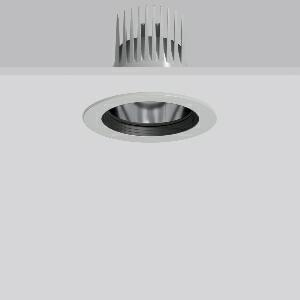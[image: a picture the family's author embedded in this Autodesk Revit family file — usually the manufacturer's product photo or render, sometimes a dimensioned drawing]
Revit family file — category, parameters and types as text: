
# Revit family: heledon_maxi_e_901759_004_2_2500
name_source: partatom
category: Lighting Fixtures
units: mm (PartAtom-declared; Revit-internal decimal feet)

## family parameters
Cut with Voids When Loaded = No
Host = Face
Light Source = No
Part Type = Normal
Room Calculation Point = No
Round Connector Dimension = Use Diameter
Shared = No

## types (1)
- HELEDON maxi E (1 x LED Modul 927, 3050 lm, 2700)
    Apparent Load = 25 VA
    Approval mark = CE
    CIE Flux Codes = 97 100 100 100 100
    Color Rendering = 92
    Color Temperature = 2700
    Default Elevation = 1800 mm
    Description = Series: HELEDON maxi
Round recessed downlight. Housing: die-cast aluminium, powder-coated. Black plastic ring and recessed LED to prevent glare from the side. Optical assembly with reflector made of MIRO-Silver with 98% total light reflection for outstanding efficiency - can be changed without tools. Best colour rendering index Ra>90. Suitable for Recessed ceiling mounting. Installation without tools thanks to spring fastening system. Including separate LED converter with connecting cable 600 mm.High quality converter without flickering and stroboscopic effect. Through-wiring box (5 pole) available as accessory. The following accessories can be mounted without use of tools: interchangeable lenses, decorative glasses, honeycomb louvre, clear and frosted diffusers, white interchangeable plastic ring. 
Colour: silver
Diameter: 162 mm
Height: 3 mm
Cut-out diameter: 152 mm
Recess height: 200 mm
Luminaire: recess height: 135 mm
Lamp: LED
Socket: without socket
Colour temperature: 2700K
Colour rendering index (CRI): 92
System power: 25 W
Rated luminous flux: 3050 lm
Luminous efficiency: 122 lm/W
Control gear: Regulated power supply
Protection class: II
Type of protection: IP 20
    Height = 0 mm  [stored 0 ft]
    Lamp = 1 x LED Modul 927
    Lamp Light Flux = 3050 lm
    Lamp count = 1
    Length = 162 mm
    Lifetime = 50000 h
    Luminous efficacy = 122 lm/W
    Manufacturer = RZB
    ModVariant = No
    Model = 901759.004.2
    Mounting Place = Ceiling
    Mounting Type = Recessed
    Number of Poles = 1
    OnlyDefault = Yes
    Power Factor = 1
    Product Name = HELEDON maxi E
    Product group = Recessed downlights
    ProductGroupID = 402
    Protection Class = Protection class II
    Protection Degree = IP 20
    RLX_Detail_Level = 1
    RLX_Emergency_Light_Flux = 0 lm
    RLX_Emergency_Type = 0
    RLX_Emergency_Type_DB = No
    RlxData = <blob elided: 118725 chars, md5=e2c16438>
    Socket = socket
    Standby Power = 0 W
    System Light Flux = 3050 lm
    System Power = 25 W
    Type Comments = Product without accessories
    Type Image = 901662.004.jpg
    URL = http://relux.com
    VarID = ---
    Voltage = 230 V
    Voltage Range = 220-240 V
    Weight = 0.00 kg
    Width = 0 mm  [stored 0 ft]

note: [stored X ft] marks values corroborated as IEEE doubles in the binary element streams (Revit-internal decimal feet)

## geometry (parser evidence)
native form markers: Blend x4, Sweep x11
no freeform markers — native parametric forms only
